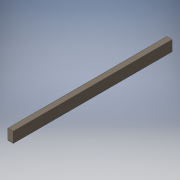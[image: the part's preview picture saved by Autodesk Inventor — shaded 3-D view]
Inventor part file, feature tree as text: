
AUTODESK INVENTOR PART (.ipt)
format: ipt  version: 2016 (Build 200138000, 138)  size: 93,696 bytes
history: native  units: in
note: dims shown in document units (in); Inventor stores cm internally (conversion verified against a paired STEP export)
features: extrude x1, sketch x1
ambient origin geometry x8: Origin, YZ Plane, XZ Plane, XY Plane, X Axis, Y Axis, Z Axis, Center Point
bodies: Solid1 (feature_tree)
feature tree (2):
  extrude  "Extrusion1"  Depth=4.0in
  sketch  "Sketch1"  dims[d0=2.0in d1=4.0in d2=60.0in d3=0.0in]
